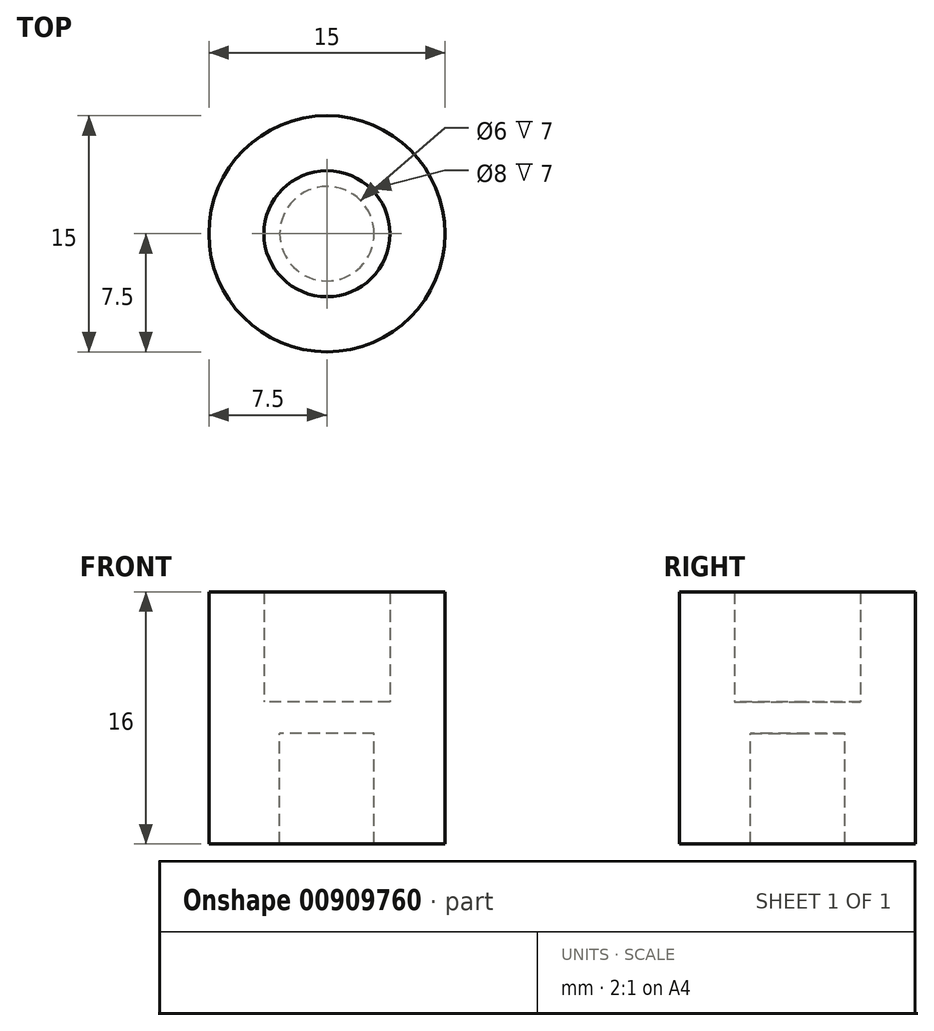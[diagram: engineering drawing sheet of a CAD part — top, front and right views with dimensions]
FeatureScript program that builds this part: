
annotation { "Feature Type Name" : "Feature", "Feature Type Description" : "" }
export const myFeature = defineFeature(function(context is Context, id is Id, definition is map)
    precondition{}
    {
        {
            var Q0;
            Q0=qCreatedBy(makeId("Top.planeOp"),FACE);
            var sketch = newSketch(context, id + "F0", { "sketchPlane" : qUnion([Q0])});
            skCircle(sketch, "E0", {"center": v(0, 0) * mm, "radius": 7.5 * mm});
            skCircle(sketch, "E1", {"center": v(0, 0) * mm, "radius": 4 * mm});
            skCircle(sketch, "E2", {"center": v(0, 0) * mm, "radius": 3 * mm});
            skSolve(sketch);
        }
        {
            var Q0;
            Q0 = qSketchRegion(id + "F0", true);
            extrude(context, id + "F1", {"entities" : qUnion([Q0]), "depth" : 8 * mm, "offsetDistance" : 25 * mm});
        }
        {
            var Q0;
            Q0=makeQuery(id+"F0.imprint","IMPRINT",FACE,{"disambiguationData":[TD([[makeQuery(id+"F0.imprint","IMPRINT",EDGE,{"derivedFrom":sQuery(id+"F0.wireOp",EDGE,"E1")}),1.0]])]});
            var Q1;
            Q1=makeQuery(id+"F0.imprint","IMPRINT",FACE,{"disambiguationData":[TD([[makeQuery(id+"F0.imprint","IMPRINT",EDGE,{"derivedFrom":sQuery(id+"F0.wireOp",EDGE,"E0")}),1.0]])]});
            extrude(context, id + "F2", {"entities" : qUnion([Q0, Q1]), "operationType" : NewBodyOperationType.ADD, "oppositeDirection" : true, "depth" : 8 * mm, "offsetDistance" : 25 * mm});
        }
        {
            var Q0;
            Q0=makeQuery(id+"F0.imprint","IMPRINT",FACE,{"disambiguationData":[TD([[makeQuery(id+"F0.imprint","IMPRINT",EDGE,{"derivedFrom":sQuery(id+"F0.wireOp",EDGE,"E2")}),1.0]])]});
            var Q1;
            Q1=makeQuery(id+"F0.imprint","IMPRINT",FACE,{"disambiguationData":[TD([[makeQuery(id+"F0.imprint","IMPRINT",EDGE,{"derivedFrom":sQuery(id+"F0.wireOp",EDGE,"E1")}),1.0]])]});
            extrude(context, id + "F3", {"entities" : qUnion([Q0, Q1]), "operationType" : NewBodyOperationType.ADD, "depth" : 1 * mm, "offsetDistance" : 25 * mm, "hasSecondDirection" : true, "secondDirectionOppositeDirection" : true, "secondDirectionDepth" : 1 * mm});
        }
    });
